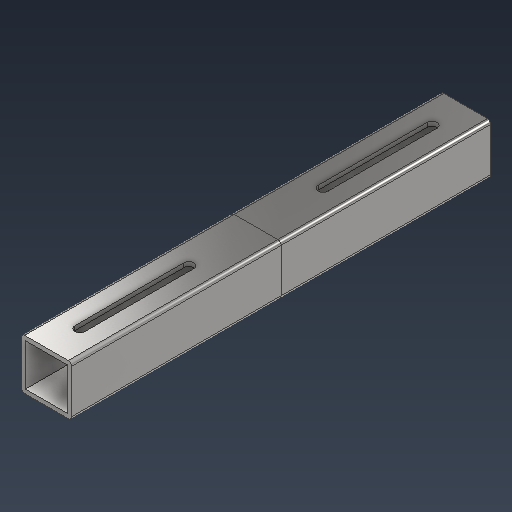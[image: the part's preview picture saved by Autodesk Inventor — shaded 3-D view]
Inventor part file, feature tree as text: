
AUTODESK INVENTOR PART (.ipt)
format: ipt  version: 2021 (Build 250183000, 183)  size: 253,440 bytes
history: native  units: mm
features: extrude x2, split x2, sketch x2, fillet x1, plane x1, other x1
ambient origin geometry x8: Origin, YZ Plane, XZ Plane, XY Plane, X Axis, Y Axis, Z Axis, Center Point
bodies: Solid1 (feature_tree), Solid4 (feature_tree), Solid5 (feature_tree)
feature tree (9):
  extrude  "Extrusion1"  Depth=30.0mm
  fillet  "Fillet1"  Radius=15.0mm
  plane  "Work Plane1"
  split  "Split1"
  other  "midPlane"
  extrude  "Extrusion2"  Depth=2.5mm
  split  "Split3"
  sketch  "Sketch1"  dims[d0=30.0mm d1=30.0mm d2=15.0mm]
  sketch  "Sketch3"  dims[d3=15.0mm d4=2.5mm d5=1000.0mm d6=0.0mm d7=2.0mm d8=-250.0mm d28=6.0mm d29=6.0mm d30=30.0mm d31=15.0mm d32=15.0mm d33=65.0mm d34=65.0mm d35=20.0mm d36=20.0mm d37=0.0mm d38=0.0mm]
